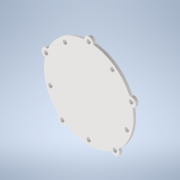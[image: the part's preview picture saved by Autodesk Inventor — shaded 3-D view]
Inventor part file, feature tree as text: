
AUTODESK INVENTOR PART (.ipt)
format: ipt  version: 2022 (Build 260153000, 153)  size: 149,504 bytes
history: native  units: mm
features: sketch x2, extrude x1
ambient origin geometry x8: Origin, YZ Plane, XZ Plane, XY Plane, X Axis, Y Axis, Z Axis, Center Point
bodies: Solid1 (feature_tree)
feature tree (3):
  sketch  "Sketch1"  dims[d0=98.0mm d1=5.0mm]
  extrude  "BaseSuelo"  Depth=5.0mm
  sketch  "Sketch2"  dims[d2=4.8mm d3=50.0mm d5=360.0deg d7=10.0mm d8=4.8mm d9=50.0mm d11=360.0deg d13=3.0mm d14=0.0mm]
